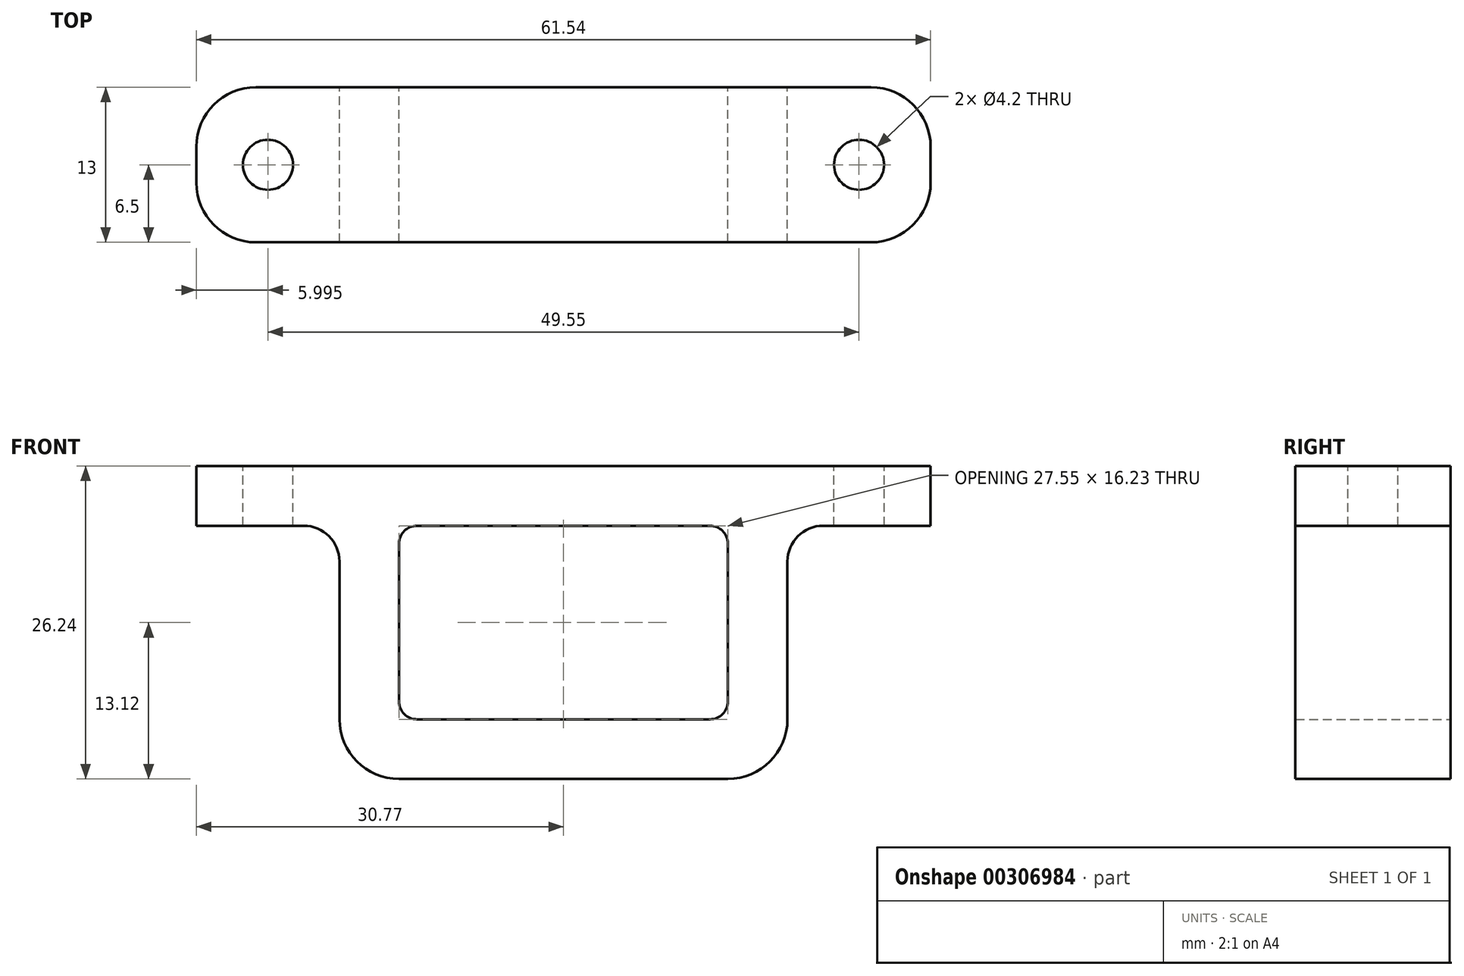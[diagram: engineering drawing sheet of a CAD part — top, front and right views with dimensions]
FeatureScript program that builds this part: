
annotation { "Feature Type Name" : "Feature", "Feature Type Description" : "" }
export const myFeature = defineFeature(function(context is Context, id is Id, definition is map)
    precondition{}
    {
        {
            var Q0;
            Q0=qCreatedBy(makeId("Front.planeOp"),FACE);
            var sketch = newSketch(context, id + "F0", { "sketchPlane" : qUnion([Q0])});
            skLineSegment(sketch, "E0.bottom", {"start": v(13.78, -8.11) * mm, "end": v(-13.77, -8.12) * mm});
            skLineSegment(sketch, "E0.top", {"start": v(13.77, 8.12) * mm, "end": v(-13.78, 8.11) * mm});
            skLineSegment(sketch, "E0.left", {"start": v(13.78, -8.11) * mm, "end": v(13.78, 8.12) * mm});
            skLineSegment(sketch, "E0.right", {"start": v(-13.78, -8.12) * mm, "end": v(-13.78, 8.11) * mm});
            skPoint(sketch, "E0.middle", {"position": v(0, 0) * mm});
            skLineSegment(sketch, "E1.bottom", {"start": v(18.78, -13.12) * mm, "end": v(-18.77, -13.12) * mm});
            skLineSegment(sketch, "E1.top", {"start": v(18.77, 13.12) * mm, "end": v(-18.78, 13.11) * mm});
            skLineSegment(sketch, "E1.left", {"start": v(18.77, -13.12) * mm, "end": v(18.77, 13.12) * mm});
            skLineSegment(sketch, "E1.right", {"start": v(-18.77, -13.12) * mm, "end": v(-18.77, 13.12) * mm});
            skSolve(sketch);
        }
        {
            var Q0;
            Q0 = qSketchRegion(id + "F0", true);
            extrude(context, id + "F1", {"entities" : qUnion([Q0]), "depth" : 13 * mm});
        }
        {
            var Q0;
            Q0=makeQuery(id+"F1.opExtrude","SWEPT_FACE",FACE,{"disambiguationData":[OSD([sQuery(id+"F0.wireOp",EDGE,"E1.top")])]});
            var sketch = newSketch(context, id + "F2", { "sketchPlane" : qUnion([Q0])});
            skPoint(sketch, "E2.oppositeSnap0", {"position": v(0, -13) * mm});
            skLineSegment(sketch, "E2.bottom", {"start": v(30.77, 0) * mm, "end": v(-30.78, 0) * mm});
            skLineSegment(sketch, "E2.top", {"start": v(30.78, -13) * mm, "end": v(-30.77, -13) * mm});
            skLineSegment(sketch, "E2.left", {"start": v(30.77, 0) * mm, "end": v(30.77, -13) * mm});
            skLineSegment(sketch, "E2.right", {"start": v(-30.78, 0) * mm, "end": v(-30.77, -13) * mm});
            skCircle(sketch, "E3", {"center": v(-24.78, -6.5) * mm, "radius": 2.1 * mm});
            skLineSegment(sketch, "E4", {"start": v(-30.78, 0) * mm, "end": v(-18.77, -13) * mm, "construction": true});
            skLineSegment(sketch, "E5", {"start": v(-18.77, -13) * mm, "end": v(-18.77, 0) * mm, "construction": true});
            skLineSegment(sketch, "E6", {"start": v(-18.77, 0) * mm, "end": v(-30.77, -13) * mm, "construction": true});
            skLineSegment(sketch, "E7", {"start": v(30.77, 0) * mm, "end": v(18.77, -13) * mm, "construction": true});
            skLineSegment(sketch, "E8", {"start": v(18.77, -13) * mm, "end": v(30.78, -13) * mm, "construction": true});
            skLineSegment(sketch, "E9", {"start": v(18.77, 0) * mm, "end": v(30.77, -13) * mm, "construction": true});
            skCircle(sketch, "E10", {"center": v(24.77, -6.5) * mm, "radius": 2.1 * mm});
            skSolve(sketch);
        }
        {
            var Q0;
            Q0 = qSketchRegion(id + "F2", true);
            extrude(context, id + "F3", {"entities" : qUnion([Q0]), "operationType" : NewBodyOperationType.ADD, "oppositeDirection" : true, "depth" : 5 * mm});
        }
        {
            var Q0;
            Q0=makeQuery(id+"F3.boolean.opBoolean","INTERSECT",EDGE,{"derivedFrom":[makeQuery(id+"F1.opExtrude","SWEPT_FACE",FACE,{"disambiguationData":[OSD([sQuery(id+"F0.wireOp",EDGE,"E1.right")])]}),makeQuery(id+"F3.opExtrude","CAP_FACE",FACE,{"disambiguationData":[OSD([sQuery(id+"F2.wireOp",EDGE,"E2.bottom"),sQuery(id+"F2.wireOp",EDGE,"E2.top"),sQuery(id+"F2.wireOp",EDGE,"E2.left"),sQuery(id+"F2.wireOp",EDGE,"E2.right"),sQuery(id+"F2.wireOp",EDGE,"E3"),sQuery(id+"F2.wireOp",EDGE,"E10")])],"isStart":false})]});
            var Q1;
            Q1=makeQuery(id+"F3.boolean.opBoolean","INTERSECT",EDGE,{"derivedFrom":[makeQuery(id+"F1.opExtrude","SWEPT_FACE",FACE,{"disambiguationData":[OSD([sQuery(id+"F0.wireOp",EDGE,"E1.left")])]}),makeQuery(id+"F3.opExtrude","CAP_FACE",FACE,{"disambiguationData":[OSD([sQuery(id+"F2.wireOp",EDGE,"E2.bottom"),sQuery(id+"F2.wireOp",EDGE,"E2.top"),sQuery(id+"F2.wireOp",EDGE,"E2.left"),sQuery(id+"F2.wireOp",EDGE,"E2.right"),sQuery(id+"F2.wireOp",EDGE,"E3"),sQuery(id+"F2.wireOp",EDGE,"E10")])],"isStart":false})]});
            fillet(context, id + "F4", {"entities" : qUnion([Q0, Q1]), "radius" : 3 * mm, "tangentPropagation" : true, "allowEdgeOverflow" : false});
        }
        {
            var Q0;
            Q0=makeQuery(id+"F1.opExtrude","SWEPT_EDGE",EDGE,{"disambiguationData":[OSD([sQuery(id+"F0.wireOp",EDGE,"E0.top"),sQuery(id+"F0.wireOp",EDGE,"E0.right")])]});
            var Q1;
            Q1=makeQuery(id+"F1.opExtrude","SWEPT_EDGE",EDGE,{"disambiguationData":[OSD([sQuery(id+"F0.wireOp",EDGE,"E0.top"),sQuery(id+"F0.wireOp",EDGE,"E0.left")])]});
            var Q2;
            Q2=makeQuery(id+"F1.opExtrude","SWEPT_EDGE",EDGE,{"disambiguationData":[OSD([sQuery(id+"F0.wireOp",EDGE,"E0.bottom"),sQuery(id+"F0.wireOp",EDGE,"E0.left")])]});
            var Q3;
            Q3=makeQuery(id+"F1.opExtrude","SWEPT_EDGE",EDGE,{"disambiguationData":[OSD([sQuery(id+"F0.wireOp",EDGE,"E0.bottom"),sQuery(id+"F0.wireOp",EDGE,"E0.right")])]});
            fillet(context, id + "F5", {"entities" : qUnion([Q0, Q1, Q2, Q3]), "radius" : 1.5 * mm, "tangentPropagation" : true, "allowEdgeOverflow" : false});
        }
        {
            var Q0;
            Q0=makeQuery(id+"F1.opExtrude","SWEPT_EDGE",EDGE,{"disambiguationData":[OSD([sQuery(id+"F0.wireOp",EDGE,"E1.bottom"),sQuery(id+"F0.wireOp",EDGE,"E1.left")])]});
            var Q1;
            Q1=makeQuery(id+"F1.opExtrude","SWEPT_EDGE",EDGE,{"disambiguationData":[OSD([sQuery(id+"F0.wireOp",EDGE,"E1.bottom"),sQuery(id+"F0.wireOp",EDGE,"E1.right")])]});
            fillet(context, id + "F6", {"entities" : qUnion([Q0, Q1]), "radius" : 5 * mm, "tangentPropagation" : true, "allowEdgeOverflow" : false});
        }
        {
            var Q0;
            Q0=makeQuery(id+"F3.opExtrude","SWEPT_EDGE",EDGE,{"disambiguationData":[OSD([sQuery(id+"F2.wireOp",EDGE,"E2.top"),sQuery(id+"F2.wireOp",EDGE,"E2.left")])]});
            var Q1;
            Q1=makeQuery(id+"F3.opExtrude","SWEPT_EDGE",EDGE,{"disambiguationData":[OSD([sQuery(id+"F2.wireOp",EDGE,"E2.bottom"),sQuery(id+"F2.wireOp",EDGE,"E2.left")])]});
            var Q2;
            Q2=makeQuery(id+"F3.opExtrude","SWEPT_EDGE",EDGE,{"disambiguationData":[OSD([sQuery(id+"F2.wireOp",EDGE,"E2.top"),sQuery(id+"F2.wireOp",EDGE,"E2.right")])]});
            var Q3;
            Q3=makeQuery(id+"F3.opExtrude","SWEPT_EDGE",EDGE,{"disambiguationData":[OSD([sQuery(id+"F2.wireOp",EDGE,"E2.bottom"),sQuery(id+"F2.wireOp",EDGE,"E2.right")])]});
            fillet(context, id + "F7", {"entities" : qUnion([Q0, Q1, Q2, Q3]), "radius" : 5 * mm, "tangentPropagation" : true, "allowEdgeOverflow" : false});
        }
    });
